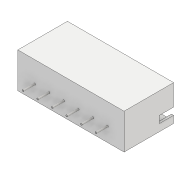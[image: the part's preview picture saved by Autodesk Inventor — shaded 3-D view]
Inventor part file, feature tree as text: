
AUTODESK INVENTOR PART (.ipt)
format: ipt  version: 2018 (Build 220112000, 112)  size: 187,392 bytes
history: native  units: mm
features: extrude x5, sketch x5, mirror x3, projected_geometry x3, pattern_linear x1
ambient origin geometry x8: Origin, YZ Plane, XZ Plane, XY Plane, X Axis, Y Axis, Z Axis, Center Point
bodies: Solid1 (feature_tree)
feature tree (17):
  extrude  "Extrusion1"  Depth=5.0mm
  extrude  "Extrusion2"  Depth=0.3mm
  mirror  "Mirror1"
  extrude  "Extrusion3"  Depth=0.3mm
  mirror  "Mirror2"
  extrude  "Extrusion4"  Depth=1.25mm
  pattern_linear  "Rectangular Pattern1"  Spacing1=0.5mm  [1 undecoded]
  extrude  "Extrusion5"  Depth=0.5mm
  mirror  "Mirror3"
  sketch  "Sketch1"  dims[d0=15.0mm d1=5.0mm]
  sketch  "Sketch2"  dims[d2=1.0mm d3=0.0mm d4=0.3mm]
  projected_geometry  "Projected Loop1"
  sketch  "Sketch3"  dims[d5=0.3mm d6=0.3mm]
  projected_geometry  "Projected Loop2"
  sketch  "Sketch4"  dims[d7=6.0mm d8=0.0mm d9=1.25mm]
  sketch  "Sketch5"  dims[d10=2.5mm d11=0.5mm d12=0.5mm d13=6.0mm d14=0.0mm d15=0.25mm d16=0.5mm d17=14.4mm d18=2.057143mm d19=5.25mm d20=0.0mm d21=60.0mm d23=2.057143mm d24=2.625mm d25=0.0mm d26=1.0mm d27=2.0mm d28=1.0mm d29=5.25mm d30=0.0mm]
  projected_geometry  "Projected Loop3"
note: 1 required parameter value undecoded (feature->parameter linkage not recoverable at this tier; creation-order binding heuristic only, values carry confidence <= 0.55)
